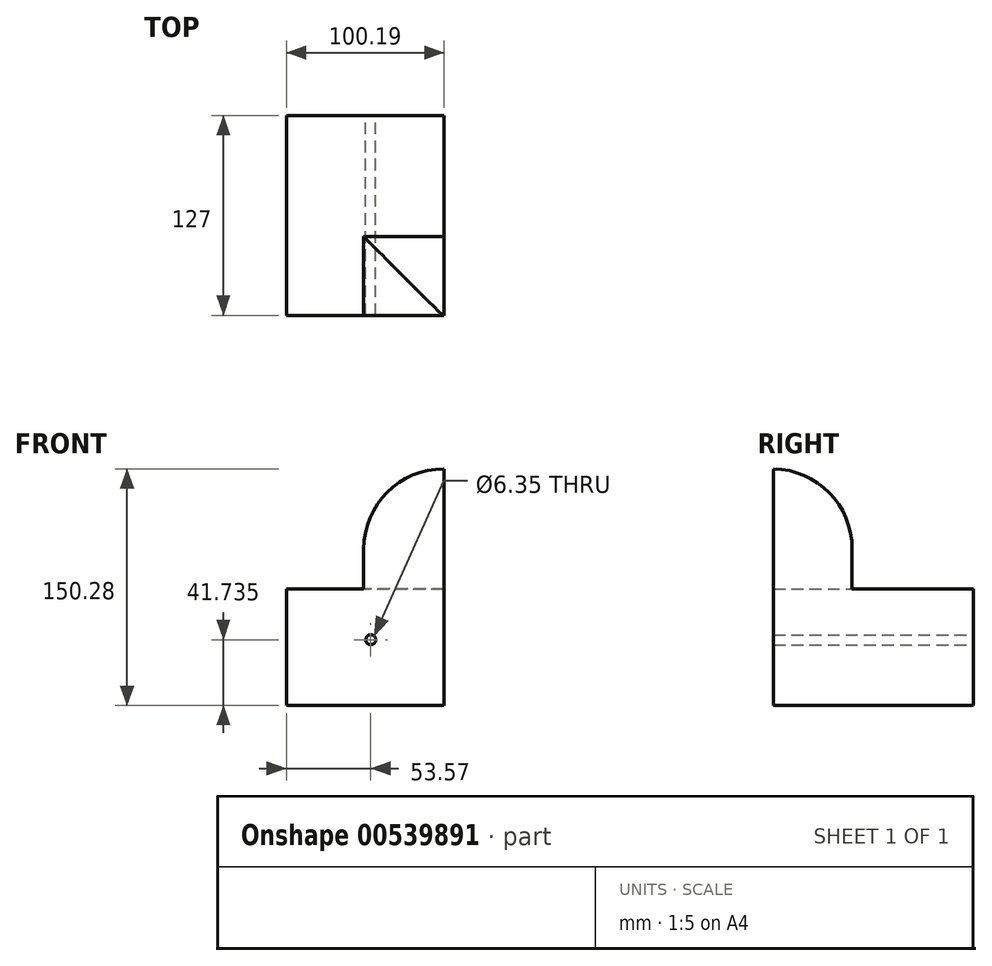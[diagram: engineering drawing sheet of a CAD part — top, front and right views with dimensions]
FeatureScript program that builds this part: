
annotation { "Feature Type Name" : "Feature", "Feature Type Description" : "" }
export const myFeature = defineFeature(function(context is Context, id is Id, definition is map)
    precondition{}
    {
        {
            var Q0;
            Q0=qCreatedBy(makeId("Front.planeOp"),FACE);
            var sketch = newSketch(context, id + "F0", { "sketchPlane" : qUnion([Q0])});
            skLineSegment(sketch, "E0.bottom", {"start": v(0, 0) * mm, "end": v(100.19, 0) * mm});
            skLineSegment(sketch, "E0.top", {"start": v(0, 74.08) * mm, "end": v(100.19, 74.08) * mm});
            skLineSegment(sketch, "E0.left", {"start": v(0, 0) * mm, "end": v(0, 74.08) * mm});
            skLineSegment(sketch, "E0.right", {"start": v(100.19, 0) * mm, "end": v(100.19, 74.08) * mm});
            skPoint(sketch, "E0.middle", {"position": v(50.1, 37.04) * mm});
            skSolve(sketch);
        }
        {
            var Q0;
            Q0=makeQuery(id+"F0.imprint","IMPRINT",FACE,{"disambiguationData":[TD([[makeQuery(id+"F0.imprint","IMPRINT",EDGE,{"derivedFrom":sQuery(id+"F0.wireOp",EDGE,"E0.bottom")}),1.0]])]});
            extrude(context, id + "F1", {"entities" : qUnion([Q0]), "depth" : 127 * mm, "offsetDistance" : 25.4 * mm});
        }
        {
            var Q0;
            Q0=makeQuery(id+"F1.opExtrude","SWEPT_FACE",FACE,{"disambiguationData":[OSD([sQuery(id+"F0.wireOp",EDGE,"E0.top")])]});
            var sketch = newSketch(context, id + "F2", { "sketchPlane" : qUnion([Q0])});
            skLineSegment(sketch, "E1.bottom", {"start": v(100.19, -127) * mm, "end": v(49.13, -127) * mm});
            skLineSegment(sketch, "E1.top", {"start": v(100.19, -77.01) * mm, "end": v(49.13, -77.01) * mm});
            skLineSegment(sketch, "E1.left", {"start": v(100.19, -127) * mm, "end": v(100.19, -77.01) * mm});
            skLineSegment(sketch, "E1.right", {"start": v(49.13, -127) * mm, "end": v(49.13, -77.01) * mm});
            skSolve(sketch);
        }
        {
            var Q0;
            Q0 = qSketchRegion(id + "F2", true);
            extrude(context, id + "F3", {"entities" : qUnion([Q0]), "operationType" : NewBodyOperationType.ADD, "depth" : 76.2 * mm, "offsetDistance" : 25.4 * mm});
        }
        {
            var Q0;
            Q0=makeQuery(id+"F3.opExtrude","CAP_EDGE",EDGE,{"disambiguationData":[OSD([sQuery(id+"F2.wireOp",EDGE,"E1.top")])],"isStart":false});
            var Q1;
            Q1=makeQuery(id+"F3.opExtrude","CAP_EDGE",EDGE,{"disambiguationData":[OSD([sQuery(id+"F2.wireOp",EDGE,"E1.right")])],"isStart":false});
            fillet(context, id + "F4", {"entities" : qUnion([Q0, Q1]), "radius" : 50.8 * mm, "tangentPropagation" : true, "allowEdgeOverflow" : false});
        }
        {
            var Q0;
            Q0=makeQuery(id+"F1.opExtrude","CAP_FACE",FACE,{"disambiguationData":[OSD([sQuery(id+"F0.wireOp",EDGE,"E0.bottom"),sQuery(id+"F0.wireOp",EDGE,"E0.top"),sQuery(id+"F0.wireOp",EDGE,"E0.left"),sQuery(id+"F0.wireOp",EDGE,"E0.right")])],"isStart":true});
            var sketch = newSketch(context, id + "F5", { "sketchPlane" : qUnion([Q0])});
            skPoint(sketch, "E2", {"position": v(-53.57, 41.74) * mm});
            skSolve(sketch);
        }
        {
            var Q0;
            Q0=sQuery(id+"F5.wireOp",VERTEX,"E2");
            var Q1;
            Q1=makeQuery(id+"F1.opExtrude","SWEPT_BODY",BODY,{"disambiguationData":[OSD([sQuery(id+"F0.wireOp",EDGE,"E0.bottom"),sQuery(id+"F0.wireOp",EDGE,"E0.top"),sQuery(id+"F0.wireOp",EDGE,"E0.left"),sQuery(id+"F0.wireOp",EDGE,"E0.right")])]});
            hole(context, id + "F6", {"style" : HoleStyle.SIMPLE, "endStyle" : HoleEndStyle.THROUGH, "holeDiameter" : 6.35 * mm, "isTappedThrough" : true, "tappedDepth" : 12.7 * mm, "tapClearance" : 3, "locations" : qUnion([Q0]), "scope" : qUnion([Q1])});
        }
    });
